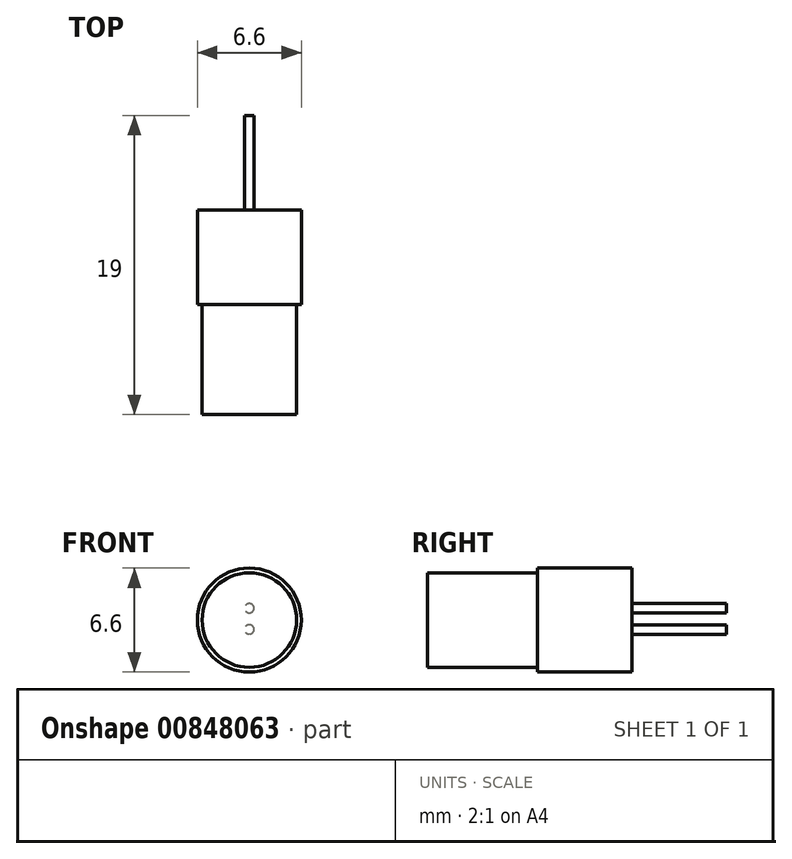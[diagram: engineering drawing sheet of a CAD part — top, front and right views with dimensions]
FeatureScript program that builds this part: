
annotation { "Feature Type Name" : "Feature", "Feature Type Description" : "" }
export const myFeature = defineFeature(function(context is Context, id is Id, definition is map)
    precondition{}
    {
        {
            var Q0;
            Q0=qCreatedBy(makeId("Front.planeOp"),FACE);
            var sketch = newSketch(context, id + "F0", { "sketchPlane" : qUnion([Q0])});
            skCircle(sketch, "E0", {"center": v(0, 0) * mm, "radius": 3 * mm});
            skCircle(sketch, "E1", {"center": v(0, 0) * mm, "radius": 3.3 * mm});
            skCircle(sketch, "E2", {"center": v(0, 0.75) * mm, "radius": 0.3 * mm});
            skCircle(sketch, "E3", {"center": v(0, -0.6) * mm, "radius": 0.3 * mm});
            skSolve(sketch);
        }
        {
            var Q0;
            Q0=makeQuery(id+"F0.imprint","IMPRINT",FACE,{"disambiguationData":[TD([[makeQuery(id+"F0.imprint","IMPRINT",EDGE,{"derivedFrom":sQuery(id+"F0.wireOp",EDGE,"E0")}),1.0]])]});
            var Q1;
            Q1=makeQuery(id+"F0.imprint","IMPRINT",FACE,{"disambiguationData":[TD([[makeQuery(id+"F0.imprint","IMPRINT",EDGE,{"derivedFrom":sQuery(id+"F0.wireOp",EDGE,"E2")}),1.0]])]});
            var Q2;
            Q2=makeQuery(id+"F0.imprint","IMPRINT",FACE,{"disambiguationData":[TD([[makeQuery(id+"F0.imprint","IMPRINT",EDGE,{"derivedFrom":sQuery(id+"F0.wireOp",EDGE,"E3")}),1.0]])]});
            extrude(context, id + "F1", {"entities" : qUnion([Q0, Q1, Q2]), "depth" : 13 * mm, "offsetDistance" : 25 * mm});
        }
        {
            var Q0;
            Q0=makeQuery(id+"F0.imprint","IMPRINT",FACE,{"disambiguationData":[TD([[makeQuery(id+"F0.imprint","IMPRINT",EDGE,{"derivedFrom":sQuery(id+"F0.wireOp",EDGE,"E0")}),-1.0]])]});
            extrude(context, id + "F2", {"entities" : qUnion([Q0]), "operationType" : NewBodyOperationType.ADD, "depth" : 6 * mm, "offsetDistance" : 25 * mm});
        }
        {
            var Q0;
            Q0=makeQuery(id+"F0.imprint","IMPRINT",FACE,{"disambiguationData":[TD([[makeQuery(id+"F0.imprint","IMPRINT",EDGE,{"derivedFrom":sQuery(id+"F0.wireOp",EDGE,"E2")}),1.0]])]});
            var Q1;
            Q1=makeQuery(id+"F0.imprint","IMPRINT",FACE,{"disambiguationData":[TD([[makeQuery(id+"F0.imprint","IMPRINT",EDGE,{"derivedFrom":sQuery(id+"F0.wireOp",EDGE,"E3")}),1.0]])]});
            extrude(context, id + "F3", {"entities" : qUnion([Q0, Q1]), "oppositeDirection" : true, "depth" : 6 * mm, "offsetDistance" : 25 * mm});
        }
    });
